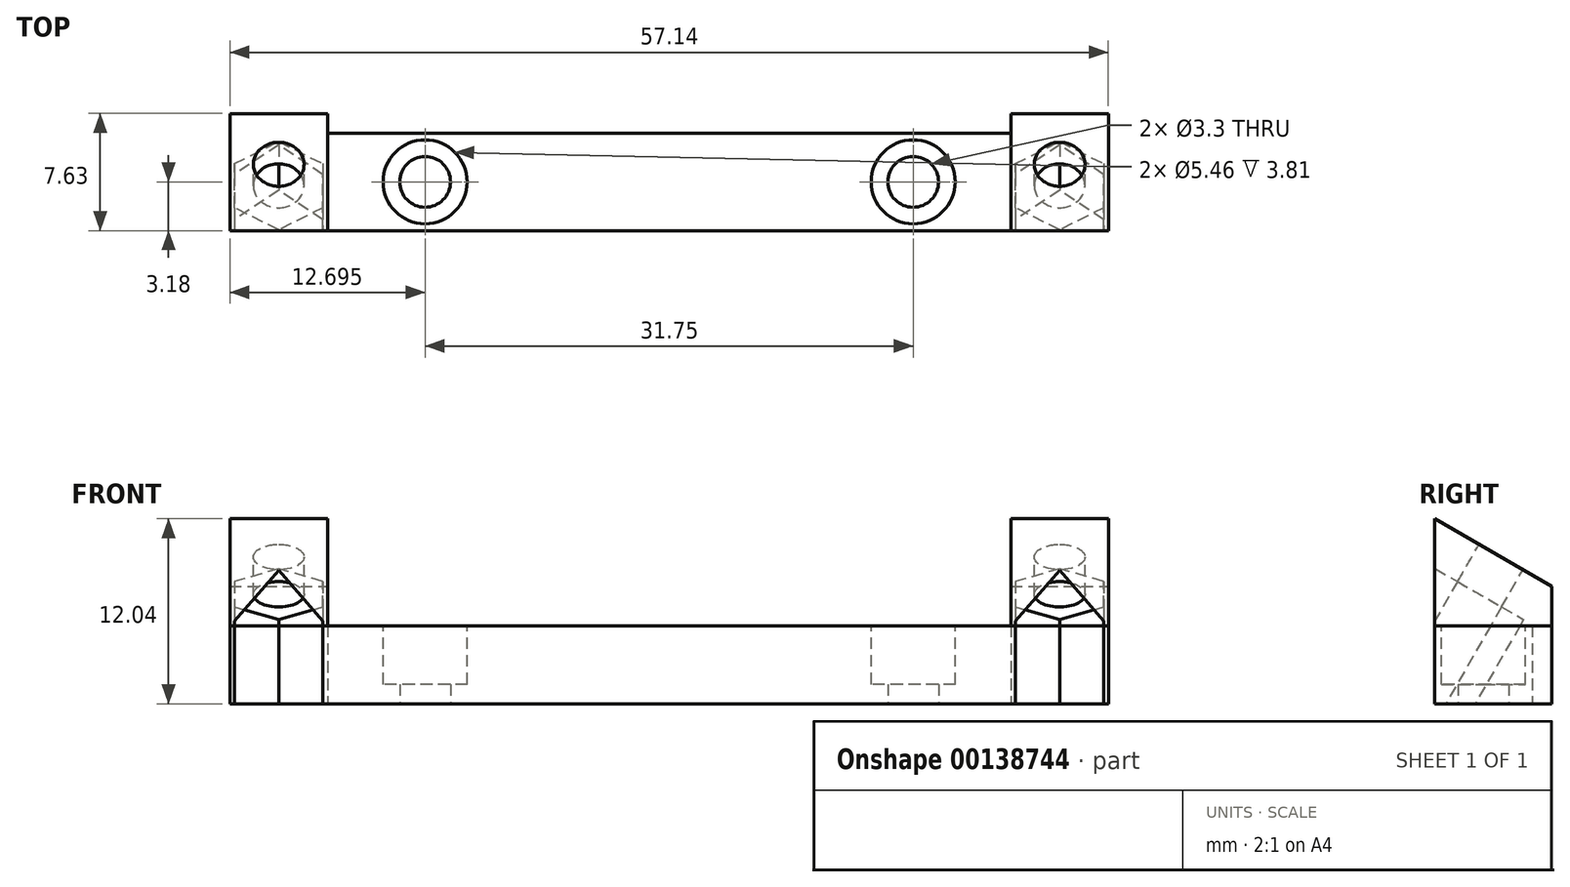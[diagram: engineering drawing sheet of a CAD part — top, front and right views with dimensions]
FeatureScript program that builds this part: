
annotation { "Feature Type Name" : "Feature", "Feature Type Description" : "" }
export const myFeature = defineFeature(function(context is Context, id is Id, definition is map)
    precondition{}
    {
        {
            var Q0;
            Q0=qCreatedBy(makeId("Top.planeOp"),FACE);
            var sketch = newSketch(context, id + "F0", { "sketchPlane" : qUnion([Q0])});
            skLineSegment(sketch, "E0.bottom", {"start": v(28.58, -3.18) * mm, "end": v(-28.58, -3.17) * mm});
            skLineSegment(sketch, "E0.top", {"start": v(22.23, 3.17) * mm, "end": v(-22.23, 3.17) * mm});
            skPoint(sketch, "E0.middle", {"position": v(0, 0) * mm});
            skCircle(sketch, "E1", {"center": v(15.88, 0) * mm, "radius": 1.65 * mm});
            skCircle(sketch, "E2", {"center": v(-15.88, 0) * mm, "radius": 1.65 * mm});
            skLineSegment(sketch, "E3.top", {"start": v(-28.58, 4.45) * mm, "end": v(-22.23, 4.45) * mm});
            skLineSegment(sketch, "E3.right", {"start": v(-22.23, 3.17) * mm, "end": v(-22.23, 4.45) * mm});
            skLineSegment(sketch, "E4.top", {"start": v(28.58, 4.45) * mm, "end": v(22.23, 4.45) * mm});
            skLineSegment(sketch, "E4.right", {"start": v(22.23, 3.18) * mm, "end": v(22.23, 4.45) * mm});
            skLineSegment(sketch, "E5", {"start": v(28.58, 4.45) * mm, "end": v(28.58, -3.17) * mm});
            skLineSegment(sketch, "E6", {"start": v(-28.58, 4.45) * mm, "end": v(-28.58, -3.18) * mm});
            skSolve(sketch);
        }
        {
            var Q0;
            Q0 = qSketchRegion(id + "F0", true);
            extrude(context, id + "F1", {"entities" : qUnion([Q0]), "depth" : 5.08 * mm});
        }
        {
            var Q0;
            Q0=makeQuery(id+"F1.opExtrude","CAP_FACE",FACE,{"disambiguationData":[OSD([sQuery(id+"F0.wireOp",EDGE,"E0.bottom"),sQuery(id+"F0.wireOp",EDGE,"E0.top"),sQuery(id+"F0.wireOp",EDGE,"E1"),sQuery(id+"F0.wireOp",EDGE,"E2"),sQuery(id+"F0.wireOp",EDGE,"E3.top"),sQuery(id+"F0.wireOp",EDGE,"E3.right"),sQuery(id+"F0.wireOp",EDGE,"E4.top"),sQuery(id+"F0.wireOp",EDGE,"E4.right"),sQuery(id+"F0.wireOp",EDGE,"E5"),sQuery(id+"F0.wireOp",EDGE,"E6"),sQuery(id+"F0.wireOp",EDGE,"588c2650-f2db-4d57-a395-859ed4c48b6a"),sQuery(id+"F0.wireOp",EDGE,"e8d0fd80-d2a9-4f85-b5ed-e0f9fc0f3cee")])],"isStart":false});
            var sketch = newSketch(context, id + "F2", { "sketchPlane" : qUnion([Q0])});
            skCircle(sketch, "E7", {"center": v(-15.88, 0) * mm, "radius": 2.73 * mm});
            skCircle(sketch, "E8", {"center": v(15.88, 0) * mm, "radius": 2.73 * mm});
            skSolve(sketch);
        }
        {
            var Q0;
            Q0 = qSketchRegion(id + "F2", true);
            extrude(context, id + "F3", {"entities" : qUnion([Q0]), "operationType" : NewBodyOperationType.REMOVE, "oppositeDirection" : true, "depth" : 3.8 * mm});
        }
        {
            var Q0;
            Q0=makeQuery(id+"F1.opExtrude","SWEPT_FACE",FACE,{"disambiguationData":[OSD([sQuery(id+"F0.wireOp",EDGE,"E5")])]});
            var sketch = newSketch(context, id + "F4", { "sketchPlane" : qUnion([Q0])});
            skLineSegment(sketch, "E9.bottom", {"start": v(-3.17, 5.08) * mm, "end": v(4.45, 5.08) * mm});
            skLineSegment(sketch, "E9.left", {"start": v(-3.17, 5.08) * mm, "end": v(-3.17, 12.04) * mm});
            skLineSegment(sketch, "E9.right", {"start": v(4.45, 5.08) * mm, "end": v(4.45, 7.64) * mm});
            skLineSegment(sketch, "E10", {"start": v(4.45, 7.64) * mm, "end": v(-3.17, 12.04) * mm});
            skSolve(sketch);
        }
        {
            var Q0;
            Q0 = qSketchRegion(id + "F4", true);
            extrude(context, id + "F5", {"entities" : qUnion([Q0]), "oppositeDirection" : true, "depth" : 57.15 * mm});
        }
        {
            var Q0;
            Q0=makeQuery(id+"F5.opExtrude","SWEPT_FACE",FACE,{"disambiguationData":[OSD([sQuery(id+"F4.wireOp",EDGE,"E9.left")])]});
            var sketch = newSketch(context, id + "F6", { "sketchPlane" : qUnion([Q0])});
            skLineSegment(sketch, "E11.bottom", {"start": v(-22.23, 12.04) * mm, "end": v(22.23, 12.04) * mm});
            skLineSegment(sketch, "E11.top", {"start": v(-22.23, 5.08) * mm, "end": v(22.23, 5.08) * mm});
            skLineSegment(sketch, "E11.left", {"start": v(-22.23, 12.04) * mm, "end": v(-22.23, 5.08) * mm});
            skLineSegment(sketch, "E11.right", {"start": v(22.23, 12.04) * mm, "end": v(22.23, 5.08) * mm});
            skSolve(sketch);
        }
        {
            var Q0;
            Q0 = qSketchRegion(id + "F6", true);
            extrude(context, id + "F7", {"entities" : qUnion([Q0]), "operationType" : NewBodyOperationType.REMOVE, "endBound" : BoundingType.UP_TO_NEXT, "oppositeDirection" : true, "depth" : 25.4 * mm});
        }
        {
            var Q0;
            {var subQ0=sQuery(id+"F4.wireOp",EDGE,"E10");Q0=makeQuery(id+"F7.boolean.opBoolean","SPLIT",FACE,{"disambiguationData":[TD([makeQuery(id+"F7.opExtrude","SWEPT_FACE",FACE,{"disambiguationData":[OSD([sQuery(id+"F6.wireOp",EDGE,"E11.right")])]})])],"derivedFrom":makeQuery(id+"F5.opExtrude","SWEPT_FACE",FACE,{"disambiguationData":[OSD([subQ0])]})});}
            var sketch = newSketch(context, id + "F8", { "sketchPlane" : qUnion([Q0])});
            skCircle(sketch, "E12", {"center": v(25.4, -3.78) * mm, "radius": 1.65 * mm});
            skCircle(sketch, "E13", {"center": v(-25.4, -3.78) * mm, "radius": 1.65 * mm});
            skSolve(sketch);
        }
        {
            var Q0;
            Q0=makeQuery(id+"F8.imprint","IMPRINT",FACE,{"disambiguationData":[TD([[makeQuery(id+"F8.imprint","IMPRINT",EDGE,{"derivedFrom":sQuery(id+"F8.wireOp",EDGE,"E12")}),1.0]])]});
            var Q1;
            Q1=makeQuery(id+"F8.imprint","IMPRINT",FACE,{"disambiguationData":[TD([[makeQuery(id+"F8.imprint","IMPRINT",EDGE,{"derivedFrom":sQuery(id+"F8.wireOp",EDGE,"E13")}),1.0]])]});
            extrude(context, id + "F9", {"entities" : qUnion([Q0, Q1]), "operationType" : NewBodyOperationType.REMOVE, "oppositeDirection" : true, "depth" : 25.4 * mm});
        }
        {
            var Q0;
            {var subQ0=sQuery(id+"F4.wireOp",EDGE,"E10");Q0=makeQuery(id+"F7.boolean.opBoolean","SPLIT",FACE,{"disambiguationData":[TD([makeQuery(id+"F7.opExtrude","SWEPT_FACE",FACE,{"disambiguationData":[OSD([sQuery(id+"F6.wireOp",EDGE,"E11.right")])]})])],"derivedFrom":makeQuery(id+"F5.opExtrude","SWEPT_FACE",FACE,{"disambiguationData":[OSD([subQ0])]})});}
            cPlane(context, id + "F10", {"entities" : qUnion([Q0]), "cplaneType" : CPlaneType.OFFSET, "offset" : 12.7 * mm, "oppositeDirection" : true, "width" : 152.4 * mm, "height" : 152.4 * mm});
        }
        {
            var Q0;
            Q0=qCreatedBy(id+"F10.planeOp",FACE);
            var sketch = newSketch(context, id + "F11", { "sketchPlane" : qUnion([Q0])});
            skCircle(sketch, "E14.cCircle", {"center": v(25.4, -3.78) * mm, "radius": 2.87 * mm, "construction": true});
            skLineSegment(sketch, "E14.0", {"start": v(22.53, -2.12) * mm, "end": v(25.4, -0.47) * mm});
            skLineSegment(sketch, "E14.1", {"start": v(25.4, -0.47) * mm, "end": v(28.27, -2.12) * mm});
            skLineSegment(sketch, "E14.2", {"start": v(28.27, -2.12) * mm, "end": v(28.27, -5.44) * mm});
            skLineSegment(sketch, "E14.3", {"start": v(28.27, -5.44) * mm, "end": v(25.4, -7.1) * mm});
            skLineSegment(sketch, "E14.4", {"start": v(25.4, -7.1) * mm, "end": v(22.53, -5.44) * mm});
            skLineSegment(sketch, "E14.5", {"start": v(22.53, -5.44) * mm, "end": v(22.53, -2.12) * mm});
            skPoint(sketch, "E14.0.midPoint", {"position": v(23.96, -1.3) * mm});
            skCircle(sketch, "E15.cCircle", {"center": v(-25.4, -3.78) * mm, "radius": 2.87 * mm, "construction": true});
            skLineSegment(sketch, "E15.0", {"start": v(-28.27, -2.12) * mm, "end": v(-25.4, -0.47) * mm});
            skLineSegment(sketch, "E15.1", {"start": v(-25.4, -0.47) * mm, "end": v(-22.53, -2.12) * mm});
            skLineSegment(sketch, "E15.2", {"start": v(-22.53, -2.12) * mm, "end": v(-22.53, -5.44) * mm});
            skLineSegment(sketch, "E15.3", {"start": v(-22.53, -5.44) * mm, "end": v(-25.4, -7.1) * mm});
            skLineSegment(sketch, "E15.4", {"start": v(-25.4, -7.1) * mm, "end": v(-28.27, -5.44) * mm});
            skLineSegment(sketch, "E15.5", {"start": v(-28.27, -5.44) * mm, "end": v(-28.27, -2.12) * mm});
            skPoint(sketch, "E15.0.midPoint", {"position": v(-26.84, -1.3) * mm});
            skSolve(sketch);
        }
        {
            var Q0;
            Q0 = qSketchRegion(id + "F11", true);
            extrude(context, id + "F12", {"entities" : qUnion([Q0]), "operationType" : NewBodyOperationType.REMOVE, "depth" : 9.9 * mm});
        }
    });
